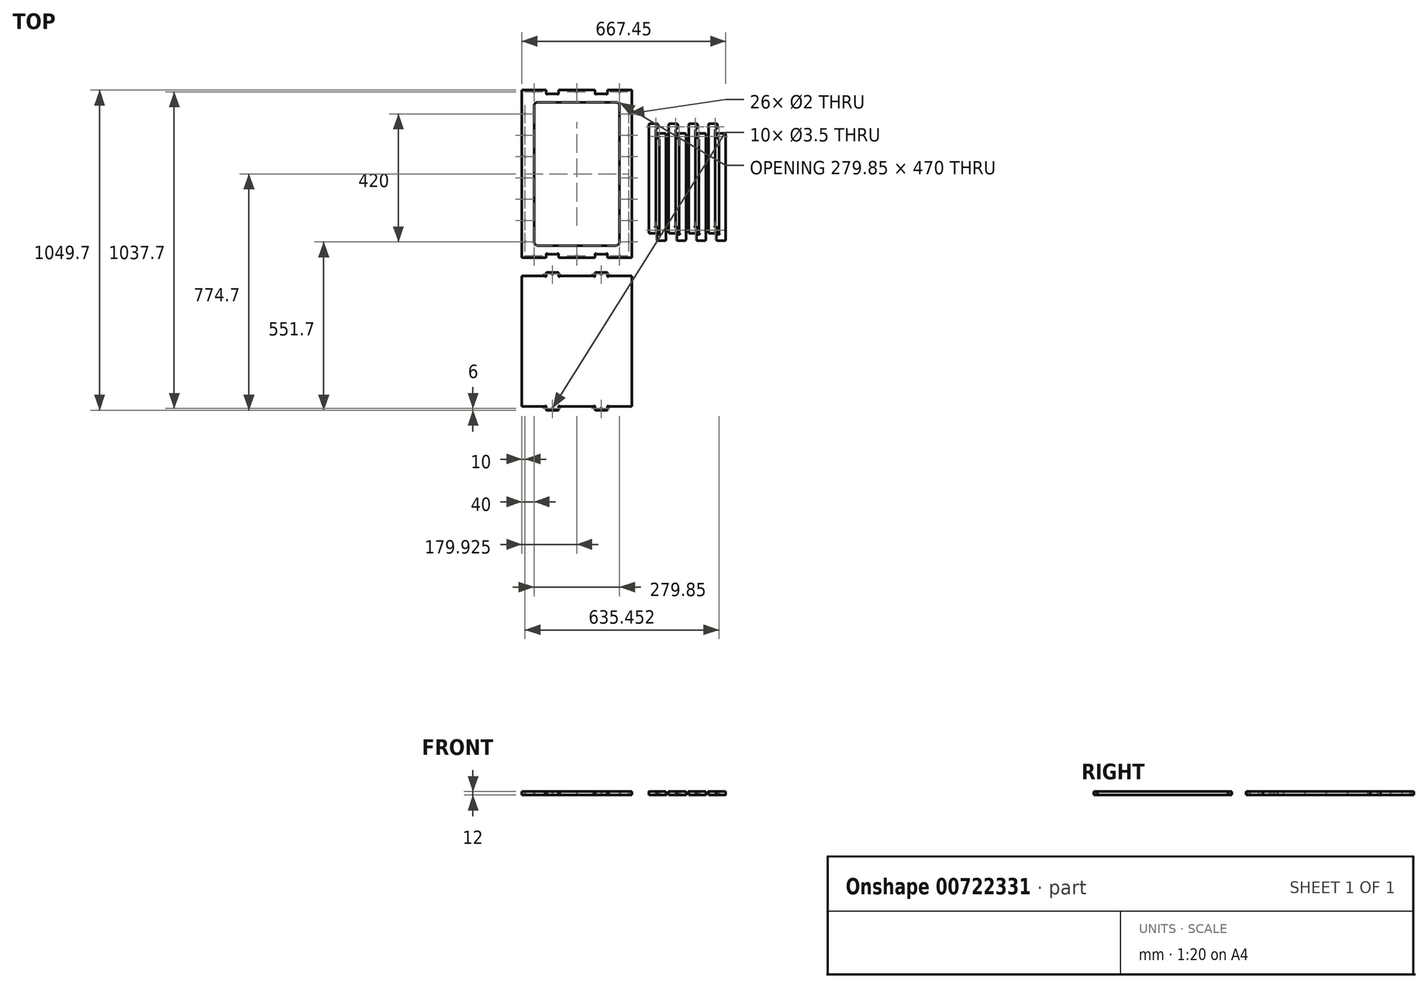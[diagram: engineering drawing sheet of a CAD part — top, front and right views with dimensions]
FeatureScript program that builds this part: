
annotation { "Feature Type Name" : "Feature", "Feature Type Description" : "" }
export const myFeature = defineFeature(function(context is Context, id is Id, definition is map)
    precondition{}
    {
        {
            var Q0;
            Q0=qCreatedBy(makeId("Top.planeOp"),FACE);
            var sketch = newSketch(context, id + "F0", { "sketchPlane" : qUnion([Q0])});
            skLineSegment(sketch, "E0.bottom", {"start": v(0, 0) * mm, "end": v(359.85, 0) * mm});
            skLineSegment(sketch, "E0.top", {"start": v(0, 550) * mm, "end": v(359.85, 550) * mm});
            skLineSegment(sketch, "E0.left", {"start": v(0, 0) * mm, "end": v(0, 550) * mm});
            skLineSegment(sketch, "E0.right", {"start": v(359.85, 0) * mm, "end": v(359.85, 550) * mm});
            skLineSegment(sketch, "E1", {"start": v(40, 550) * mm, "end": v(40, 0) * mm, "construction": true});
            skLineSegment(sketch, "E2", {"start": v(319.85, 0) * mm, "end": v(319.85, 550) * mm, "construction": true});
            skLineSegment(sketch, "E3", {"start": v(359.85, 510) * mm, "end": v(0, 510) * mm, "construction": true});
            skLineSegment(sketch, "E4", {"start": v(0, 40) * mm, "end": v(359.85, 40) * mm, "construction": true});
            skLineSegment(sketch, "E5", {"start": v(52, 510) * mm, "end": v(307.85, 510) * mm});
            skLineSegment(sketch, "E6", {"start": v(319.85, 498) * mm, "end": v(319.85, 425.14) * mm});
            skLineSegment(sketch, "E7", {"start": v(40, 425.14) * mm, "end": v(40, 498) * mm});
            skLineSegment(sketch, "E8", {"start": v(319.85, 381.14) * mm, "end": v(319.85, 52) * mm});
            skLineSegment(sketch, "E9", {"start": v(307.85, 40) * mm, "end": v(52, 40) * mm});
            skLineSegment(sketch, "E10", {"start": v(40, 52) * mm, "end": v(40, 381.14) * mm});
            skPoint(sketch, "E11.visualSharp", {"position": v(40, 510) * mm});
            skArc(sketch, "E11.filletArc", {"start": v(52, 510) * mm, "mid": v(43.51, 506.49) * mm, "end": v(40, 498) * mm});
            skPoint(sketch, "E12.visualSharp", {"position": v(319.85, 510) * mm});
            skArc(sketch, "E12.filletArc", {"start": v(319.85, 498) * mm, "mid": v(316.34, 506.49) * mm, "end": v(307.85, 510) * mm});
            skPoint(sketch, "E13.visualSharp", {"position": v(319.85, 40) * mm});
            skArc(sketch, "E13.filletArc", {"start": v(307.85, 40) * mm, "mid": v(316.34, 43.51) * mm, "end": v(319.85, 52) * mm});
            skPoint(sketch, "E14.visualSharp", {"position": v(40, 40) * mm});
            skArc(sketch, "E14.filletArc", {"start": v(40, 52) * mm, "mid": v(43.51, 43.51) * mm, "end": v(52, 40) * mm});
            skCircle(sketch, "E15", {"center": v(10, 52) * mm, "radius": 1 * mm});
            skLineSegment(sketch, "E16", {"start": v(-24.67, 52) * mm, "end": v(376.85, 52) * mm, "construction": true});
            skCircle(sketch, "E17", {"center": v(349.85, 52) * mm, "radius": 1 * mm});
            skCircle(sketch, "E18.0.1.0", {"center": v(10, 122) * mm, "radius": 1 * mm});
            skCircle(sketch, "E18.0.1.1", {"center": v(349.85, 122) * mm, "radius": 1 * mm});
            skCircle(sketch, "E18.0.2.0", {"center": v(10, 192) * mm, "radius": 1 * mm});
            skCircle(sketch, "E18.0.2.1", {"center": v(349.85, 192) * mm, "radius": 1 * mm});
            skCircle(sketch, "E18.0.3.0", {"center": v(10, 262) * mm, "radius": 1 * mm});
            skCircle(sketch, "E18.0.3.1", {"center": v(349.85, 262) * mm, "radius": 1 * mm});
            skCircle(sketch, "E18.0.4.0", {"center": v(10, 332) * mm, "radius": 1 * mm});
            skCircle(sketch, "E18.0.4.1", {"center": v(349.85, 332) * mm, "radius": 1 * mm});
            skCircle(sketch, "E18.0.5.0", {"center": v(10, 402) * mm, "radius": 1 * mm});
            skCircle(sketch, "E18.0.5.1", {"center": v(349.85, 402) * mm, "radius": 1 * mm});
            skCircle(sketch, "E18.0.6.0", {"center": v(10, 472) * mm, "radius": 1 * mm});
            skCircle(sketch, "E18.0.6.1", {"center": v(349.85, 472) * mm, "radius": 1 * mm});
            skLineSegment(sketch, "E18.direction1", {"start": v(10, 52) * mm, "end": v(35, 52) * mm, "construction": true});
            skLineSegment(sketch, "E18.direction2", {"start": v(10, 52) * mm, "end": v(10, 122) * mm, "construction": true});
            skLineSegment(sketch, "E19", {"start": v(80, 0) * mm, "end": v(80, 12) * mm});
            skLineSegment(sketch, "E20", {"start": v(120, 12) * mm, "end": v(120, 0) * mm});
            skLineSegment(sketch, "E21", {"start": v(239.85, 0) * mm, "end": v(239.85, 12) * mm});
            skLineSegment(sketch, "E22", {"start": v(279.85, 12) * mm, "end": v(279.85, 0) * mm});
            skLineSegment(sketch, "E23", {"start": v(80, 550) * mm, "end": v(80, 538) * mm});
            skLineSegment(sketch, "E24", {"start": v(120, 538) * mm, "end": v(120, 550) * mm});
            skLineSegment(sketch, "E25", {"start": v(239.85, 550) * mm, "end": v(239.85, 538) * mm});
            skLineSegment(sketch, "E26", {"start": v(243.85, 538) * mm, "end": v(275.85, 538) * mm});
            skLineSegment(sketch, "E27", {"start": v(279.85, 538) * mm, "end": v(279.85, 550) * mm});
            skLineSegment(sketch, "E28", {"start": v(0, 6) * mm, "end": v(359.85, 6) * mm, "construction": true});
            skCircle(sketch, "E29", {"center": v(179.93, 6) * mm, "radius": 1.75 * mm});
            skCircle(sketch, "E30", {"center": v(319.85, 6) * mm, "radius": 1.75 * mm});
            skCircle(sketch, "E31", {"center": v(40, 6) * mm, "radius": 1.75 * mm});
            skLineSegment(sketch, "E32", {"start": v(0, 544) * mm, "end": v(359.85, 544) * mm, "construction": true});
            skCircle(sketch, "E33", {"center": v(179.93, 544) * mm, "radius": 1.75 * mm});
            skCircle(sketch, "E34", {"center": v(319.85, 544) * mm, "radius": 1.75 * mm});
            skCircle(sketch, "E35", {"center": v(40, 544) * mm, "radius": 1.75 * mm});
            skArc(sketch, "E36", {"start": v(80, 12) * mm, "mid": v(82, 14) * mm, "end": v(84, 12) * mm});
            skArc(sketch, "E37", {"start": v(120, 12) * mm, "mid": v(118, 14) * mm, "end": v(116, 12) * mm});
            skArc(sketch, "E38", {"start": v(239.85, 12) * mm, "mid": v(241.85, 14) * mm, "end": v(243.85, 12) * mm});
            skArc(sketch, "E39", {"start": v(279.85, 12) * mm, "mid": v(277.85, 14) * mm, "end": v(275.85, 12) * mm});
            skLineSegment(sketch, "E40.trimOffspring", {"start": v(243.85, 12) * mm, "end": v(275.85, 12) * mm});
            skLineSegment(sketch, "E41.trimOffspring", {"start": v(84, 12) * mm, "end": v(116, 12) * mm});
            skArc(sketch, "E42", {"start": v(80, 538) * mm, "mid": v(82, 536) * mm, "end": v(84, 538) * mm});
            skArc(sketch, "E43", {"start": v(120, 538) * mm, "mid": v(118, 536) * mm, "end": v(116, 538) * mm});
            skArc(sketch, "E44", {"start": v(239.85, 538) * mm, "mid": v(241.85, 536) * mm, "end": v(243.85, 538) * mm});
            skArc(sketch, "E45", {"start": v(279.85, 538) * mm, "mid": v(277.85, 536) * mm, "end": v(275.85, 538) * mm});
            skLineSegment(sketch, "E46.trimOffspring", {"start": v(84, 538) * mm, "end": v(116, 538) * mm});
            skLineSegment(sketch, "E47", {"start": v(40, 425.14) * mm, "end": v(40, 381.14) * mm});
            skLineSegment(sketch, "E48", {"start": v(319.85, 425.14) * mm, "end": v(319.85, 381.14) * mm});
            skLineSegment(sketch, "E49", {"start": v(416.45, 83.42) * mm, "end": v(416.45, 436.47) * mm});
            skLineSegment(sketch, "E50", {"start": v(419.85, 439.87) * mm, "end": v(441.45, 439.87) * mm});
            skLineSegment(sketch, "E51", {"start": v(446.45, 434.87) * mm, "end": v(446.45, 429.28) * mm});
            skLineSegment(sketch, "E52", {"start": v(445.46, 426.87) * mm, "end": v(439.45, 420.86) * mm});
            skLineSegment(sketch, "E53", {"start": v(438.45, 418.46) * mm, "end": v(438.45, 100.02) * mm});
            skLineSegment(sketch, "E54", {"start": v(438.45, 100.02) * mm, "end": v(443.05, 100.02) * mm});
            skLineSegment(sketch, "E55", {"start": v(446.45, 96.62) * mm, "end": v(446.45, 83.42) * mm});
            skLineSegment(sketch, "E56", {"start": v(443.05, 80.02) * mm, "end": v(419.85, 80.02) * mm});
            skArc(sketch, "E57", {"start": v(438.45, 104.02) * mm, "mid": v(436.45, 102.02) * mm, "end": v(438.45, 100.02) * mm});
            skPoint(sketch, "E58.visualSharp", {"position": v(446.45, 100.02) * mm});
            skArc(sketch, "E58.filletArc", {"start": v(446.45, 96.62) * mm, "mid": v(445.46, 99.02) * mm, "end": v(443.05, 100.02) * mm});
            skPoint(sketch, "E59.visualSharp", {"position": v(446.45, 80.02) * mm});
            skArc(sketch, "E59.filletArc", {"start": v(443.05, 80.02) * mm, "mid": v(445.46, 81.01) * mm, "end": v(446.45, 83.42) * mm});
            skPoint(sketch, "E60.visualSharp", {"position": v(416.45, 80.02) * mm});
            skArc(sketch, "E60.filletArc", {"start": v(416.45, 83.42) * mm, "mid": v(417.45, 81.01) * mm, "end": v(419.85, 80.02) * mm});
            skPoint(sketch, "E61.visualSharp", {"position": v(416.45, 439.87) * mm});
            skArc(sketch, "E61.filletArc", {"start": v(419.85, 439.87) * mm, "mid": v(417.45, 438.87) * mm, "end": v(416.45, 436.47) * mm});
            skPoint(sketch, "E62.visualSharp", {"position": v(446.45, 427.87) * mm});
            skArc(sketch, "E62.filletArc", {"start": v(445.46, 426.87) * mm, "mid": v(446.2, 427.97) * mm, "end": v(446.45, 429.28) * mm});
            skPoint(sketch, "E63.visualSharp", {"position": v(438.45, 419.87) * mm});
            skArc(sketch, "E63.filletArc", {"start": v(439.45, 420.86) * mm, "mid": v(438.71, 419.76) * mm, "end": v(438.45, 418.46) * mm});
            skCircle(sketch, "E64", {"center": v(438.45, 90.02) * mm, "radius": 1 * mm});
            skPoint(sketch, "E65.visualSharp", {"position": v(446.45, 439.87) * mm});
            skArc(sketch, "E65.filletArc", {"start": v(446.45, 434.87) * mm, "mid": v(444.99, 438.4) * mm, "end": v(441.45, 439.87) * mm});
            skCircle(sketch, "E66", {"center": v(438.45, 429.87) * mm, "radius": 1 * mm});
            skLineSegment(sketch, "E67", {"start": v(445.85, 407.87) * mm, "end": v(469.05, 407.87) * mm});
            skLineSegment(sketch, "E68", {"start": v(472.45, 404.47) * mm, "end": v(472.45, 59.42) * mm});
            skLineSegment(sketch, "E69", {"start": v(469.05, 56.02) * mm, "end": v(445.85, 56.02) * mm});
            skLineSegment(sketch, "E70", {"start": v(442.45, 59.42) * mm, "end": v(442.45, 72.62) * mm});
            skLineSegment(sketch, "E71", {"start": v(445.85, 76.02) * mm, "end": v(450.45, 76.02) * mm});
            skLineSegment(sketch, "E72", {"start": v(450.45, 76.02) * mm, "end": v(450.45, 386.46) * mm});
            skLineSegment(sketch, "E73", {"start": v(449.46, 388.86) * mm, "end": v(443.45, 394.87) * mm});
            skLineSegment(sketch, "E74", {"start": v(442.45, 397.28) * mm, "end": v(442.45, 404.47) * mm});
            skPoint(sketch, "E75.visualSharp", {"position": v(442.45, 395.87) * mm});
            skArc(sketch, "E75.filletArc", {"start": v(442.45, 397.28) * mm, "mid": v(442.71, 395.97) * mm, "end": v(443.45, 394.87) * mm});
            skPoint(sketch, "E76.visualSharp", {"position": v(450.45, 387.87) * mm});
            skArc(sketch, "E76.filletArc", {"start": v(450.45, 386.46) * mm, "mid": v(450.2, 387.76) * mm, "end": v(449.46, 388.86) * mm});
            skPoint(sketch, "E77.visualSharp", {"position": v(442.45, 407.87) * mm});
            skArc(sketch, "E77.filletArc", {"start": v(445.85, 407.87) * mm, "mid": v(443.45, 406.87) * mm, "end": v(442.45, 404.47) * mm});
            skPoint(sketch, "E78.visualSharp", {"position": v(472.45, 407.87) * mm});
            skArc(sketch, "E78.filletArc", {"start": v(472.45, 404.47) * mm, "mid": v(471.46, 406.87) * mm, "end": v(469.05, 407.87) * mm});
            skPoint(sketch, "E79.visualSharp", {"position": v(472.45, 56.02) * mm});
            skArc(sketch, "E79.filletArc", {"start": v(469.05, 56.02) * mm, "mid": v(471.46, 57.01) * mm, "end": v(472.45, 59.42) * mm});
            skPoint(sketch, "E80.visualSharp", {"position": v(442.45, 56.02) * mm});
            skArc(sketch, "E80.filletArc", {"start": v(442.45, 59.42) * mm, "mid": v(443.45, 57.01) * mm, "end": v(445.85, 56.02) * mm});
            skPoint(sketch, "E81.visualSharp", {"position": v(442.45, 76.02) * mm});
            skArc(sketch, "E81.filletArc", {"start": v(445.85, 76.02) * mm, "mid": v(443.45, 75.02) * mm, "end": v(442.45, 72.62) * mm});
            skArc(sketch, "E82", {"start": v(450.45, 76.02) * mm, "mid": v(452.45, 78.02) * mm, "end": v(450.45, 80.02) * mm});
            skLineSegment(sketch, "E83.1.0.0", {"start": v(515.45, 76.02) * mm, "end": v(515.45, 386.46) * mm});
            skPoint(sketch, "E83.1.0.1", {"position": v(507.45, 56.02) * mm});
            skPoint(sketch, "E83.1.0.2", {"position": v(503.45, 419.87) * mm});
            skPoint(sketch, "E83.1.0.3", {"position": v(515.45, 387.87) * mm});
            skPoint(sketch, "E83.1.0.4", {"position": v(511.45, 80.02) * mm});
            skLineSegment(sketch, "E83.1.0.5", {"start": v(511.45, 96.62) * mm, "end": v(511.45, 83.42) * mm});
            skLineSegment(sketch, "E83.1.0.6", {"start": v(534.05, 56.02) * mm, "end": v(510.85, 56.02) * mm});
            skPoint(sketch, "E83.1.0.7", {"position": v(537.45, 56.02) * mm});
            skPoint(sketch, "E83.1.0.8", {"position": v(511.45, 427.87) * mm});
            skLineSegment(sketch, "E83.1.0.9", {"start": v(508.05, 80.02) * mm, "end": v(484.85, 80.02) * mm});
            skLineSegment(sketch, "E83.1.0.10", {"start": v(481.45, 83.42) * mm, "end": v(481.45, 436.47) * mm});
            skLineSegment(sketch, "E83.1.0.11", {"start": v(510.85, 407.87) * mm, "end": v(534.05, 407.87) * mm});
            skPoint(sketch, "E83.1.0.12", {"position": v(507.45, 76.02) * mm});
            skLineSegment(sketch, "E83.1.0.13", {"start": v(507.45, 59.42) * mm, "end": v(507.45, 72.62) * mm});
            skPoint(sketch, "E83.1.0.14", {"position": v(507.45, 407.87) * mm});
            skPoint(sketch, "E83.1.0.15", {"position": v(481.45, 80.02) * mm});
            skPoint(sketch, "E83.1.0.16", {"position": v(507.45, 395.87) * mm});
            skPoint(sketch, "E83.1.0.17", {"position": v(511.45, 100.02) * mm});
            skLineSegment(sketch, "E83.1.0.18", {"start": v(484.85, 439.87) * mm, "end": v(506.45, 439.87) * mm});
            skLineSegment(sketch, "E83.1.0.19", {"start": v(537.45, 404.47) * mm, "end": v(537.45, 59.42) * mm});
            skPoint(sketch, "E83.1.0.20", {"position": v(537.45, 407.87) * mm});
            skPoint(sketch, "E83.1.0.21", {"position": v(481.45, 439.87) * mm});
            skPoint(sketch, "E83.1.0.22", {"position": v(511.45, 439.87) * mm});
            skLineSegment(sketch, "E83.1.0.23", {"start": v(503.45, 418.46) * mm, "end": v(503.45, 100.02) * mm});
            skCircle(sketch, "E83.1.0.24", {"center": v(503.45, 429.87) * mm, "radius": 1 * mm});
            skCircle(sketch, "E83.1.0.25", {"center": v(503.45, 90.02) * mm, "radius": 1 * mm});
            skArc(sketch, "E83.1.0.26", {"start": v(534.05, 56.02) * mm, "mid": v(536.46, 57.01) * mm, "end": v(537.45, 59.42) * mm});
            skArc(sketch, "E83.1.0.27", {"start": v(507.45, 59.42) * mm, "mid": v(508.45, 57.01) * mm, "end": v(510.85, 56.02) * mm});
            skLineSegment(sketch, "E83.1.0.28", {"start": v(511.45, 434.87) * mm, "end": v(511.45, 429.28) * mm});
            skArc(sketch, "E83.1.0.29", {"start": v(508.05, 80.02) * mm, "mid": v(510.46, 81.01) * mm, "end": v(511.45, 83.42) * mm});
            skArc(sketch, "E83.1.0.30", {"start": v(515.45, 76.02) * mm, "mid": v(517.45, 78.02) * mm, "end": v(515.45, 80.02) * mm});
            skArc(sketch, "E83.1.0.31", {"start": v(511.45, 434.87) * mm, "mid": v(509.99, 438.4) * mm, "end": v(506.45, 439.87) * mm});
            skArc(sketch, "E83.1.0.32", {"start": v(537.45, 404.47) * mm, "mid": v(536.46, 406.87) * mm, "end": v(534.05, 407.87) * mm});
            skArc(sketch, "E83.1.0.33", {"start": v(481.45, 83.42) * mm, "mid": v(482.45, 81.01) * mm, "end": v(484.85, 80.02) * mm});
            skArc(sketch, "E83.1.0.34", {"start": v(503.45, 104.02) * mm, "mid": v(501.45, 102.02) * mm, "end": v(503.45, 100.02) * mm});
            skArc(sketch, "E83.1.0.35", {"start": v(484.85, 439.87) * mm, "mid": v(482.45, 438.87) * mm, "end": v(481.45, 436.47) * mm});
            skLineSegment(sketch, "E83.1.0.36", {"start": v(503.45, 100.02) * mm, "end": v(508.05, 100.02) * mm});
            skArc(sketch, "E83.1.0.37", {"start": v(510.46, 426.87) * mm, "mid": v(511.2, 427.97) * mm, "end": v(511.45, 429.28) * mm});
            skArc(sketch, "E83.1.0.38", {"start": v(515.45, 386.46) * mm, "mid": v(515.2, 387.76) * mm, "end": v(514.46, 388.86) * mm});
            skArc(sketch, "E83.1.0.39", {"start": v(511.45, 96.62) * mm, "mid": v(510.46, 99.02) * mm, "end": v(508.05, 100.02) * mm});
            skLineSegment(sketch, "E83.1.0.40", {"start": v(514.46, 388.86) * mm, "end": v(508.45, 394.87) * mm});
            skArc(sketch, "E83.1.0.41", {"start": v(510.85, 76.02) * mm, "mid": v(508.45, 75.02) * mm, "end": v(507.45, 72.62) * mm});
            skArc(sketch, "E83.1.0.42", {"start": v(504.45, 420.86) * mm, "mid": v(503.71, 419.76) * mm, "end": v(503.45, 418.46) * mm});
            skArc(sketch, "E83.1.0.43", {"start": v(510.85, 407.87) * mm, "mid": v(508.45, 406.87) * mm, "end": v(507.45, 404.47) * mm});
            skLineSegment(sketch, "E83.1.0.44", {"start": v(507.45, 397.28) * mm, "end": v(507.45, 404.47) * mm});
            skLineSegment(sketch, "E83.1.0.45", {"start": v(510.46, 426.87) * mm, "end": v(504.45, 420.86) * mm});
            skArc(sketch, "E83.1.0.46", {"start": v(507.45, 397.28) * mm, "mid": v(507.71, 395.97) * mm, "end": v(508.45, 394.87) * mm});
            skLineSegment(sketch, "E83.1.0.47", {"start": v(510.85, 76.02) * mm, "end": v(515.45, 76.02) * mm});
            skLineSegment(sketch, "E83.2.0.0", {"start": v(580.45, 76.02) * mm, "end": v(580.45, 386.46) * mm});
            skPoint(sketch, "E83.2.0.1", {"position": v(572.45, 56.02) * mm});
            skPoint(sketch, "E83.2.0.2", {"position": v(568.45, 419.87) * mm});
            skPoint(sketch, "E83.2.0.3", {"position": v(580.45, 387.87) * mm});
            skPoint(sketch, "E83.2.0.4", {"position": v(576.45, 80.02) * mm});
            skLineSegment(sketch, "E83.2.0.5", {"start": v(576.45, 96.62) * mm, "end": v(576.45, 83.42) * mm});
            skLineSegment(sketch, "E83.2.0.6", {"start": v(599.05, 56.02) * mm, "end": v(575.85, 56.02) * mm});
            skPoint(sketch, "E83.2.0.7", {"position": v(602.45, 56.02) * mm});
            skPoint(sketch, "E83.2.0.8", {"position": v(576.45, 427.87) * mm});
            skLineSegment(sketch, "E83.2.0.9", {"start": v(573.05, 80.02) * mm, "end": v(549.85, 80.02) * mm});
            skLineSegment(sketch, "E83.2.0.10", {"start": v(546.45, 83.42) * mm, "end": v(546.45, 436.47) * mm});
            skLineSegment(sketch, "E83.2.0.11", {"start": v(575.85, 407.87) * mm, "end": v(599.05, 407.87) * mm});
            skPoint(sketch, "E83.2.0.12", {"position": v(572.45, 76.02) * mm});
            skLineSegment(sketch, "E83.2.0.13", {"start": v(572.45, 59.42) * mm, "end": v(572.45, 72.62) * mm});
            skPoint(sketch, "E83.2.0.14", {"position": v(572.45, 407.87) * mm});
            skPoint(sketch, "E83.2.0.15", {"position": v(546.45, 80.02) * mm});
            skPoint(sketch, "E83.2.0.16", {"position": v(572.45, 395.87) * mm});
            skPoint(sketch, "E83.2.0.17", {"position": v(576.45, 100.02) * mm});
            skLineSegment(sketch, "E83.2.0.18", {"start": v(549.85, 439.87) * mm, "end": v(571.45, 439.87) * mm});
            skLineSegment(sketch, "E83.2.0.19", {"start": v(602.45, 404.47) * mm, "end": v(602.45, 59.42) * mm});
            skPoint(sketch, "E83.2.0.20", {"position": v(602.45, 407.87) * mm});
            skPoint(sketch, "E83.2.0.21", {"position": v(546.45, 439.87) * mm});
            skPoint(sketch, "E83.2.0.22", {"position": v(576.45, 439.87) * mm});
            skLineSegment(sketch, "E83.2.0.23", {"start": v(568.45, 418.46) * mm, "end": v(568.45, 100.02) * mm});
            skCircle(sketch, "E83.2.0.24", {"center": v(568.45, 429.87) * mm, "radius": 1 * mm});
            skCircle(sketch, "E83.2.0.25", {"center": v(568.45, 90.02) * mm, "radius": 1 * mm});
            skArc(sketch, "E83.2.0.26", {"start": v(599.05, 56.02) * mm, "mid": v(601.46, 57.01) * mm, "end": v(602.45, 59.42) * mm});
            skArc(sketch, "E83.2.0.27", {"start": v(572.45, 59.42) * mm, "mid": v(573.45, 57.01) * mm, "end": v(575.85, 56.02) * mm});
            skLineSegment(sketch, "E83.2.0.28", {"start": v(576.45, 434.87) * mm, "end": v(576.45, 429.28) * mm});
            skArc(sketch, "E83.2.0.29", {"start": v(573.05, 80.02) * mm, "mid": v(575.46, 81.01) * mm, "end": v(576.45, 83.42) * mm});
            skArc(sketch, "E83.2.0.30", {"start": v(580.45, 76.02) * mm, "mid": v(582.45, 78.02) * mm, "end": v(580.45, 80.02) * mm});
            skArc(sketch, "E83.2.0.31", {"start": v(576.45, 434.87) * mm, "mid": v(574.99, 438.4) * mm, "end": v(571.45, 439.87) * mm});
            skArc(sketch, "E83.2.0.32", {"start": v(602.45, 404.47) * mm, "mid": v(601.46, 406.87) * mm, "end": v(599.05, 407.87) * mm});
            skArc(sketch, "E83.2.0.33", {"start": v(546.45, 83.42) * mm, "mid": v(547.45, 81.01) * mm, "end": v(549.85, 80.02) * mm});
            skArc(sketch, "E83.2.0.34", {"start": v(568.45, 104.02) * mm, "mid": v(566.45, 102.02) * mm, "end": v(568.45, 100.02) * mm});
            skArc(sketch, "E83.2.0.35", {"start": v(549.85, 439.87) * mm, "mid": v(547.45, 438.87) * mm, "end": v(546.45, 436.47) * mm});
            skLineSegment(sketch, "E83.2.0.36", {"start": v(568.45, 100.02) * mm, "end": v(573.05, 100.02) * mm});
            skArc(sketch, "E83.2.0.37", {"start": v(575.46, 426.87) * mm, "mid": v(576.2, 427.97) * mm, "end": v(576.45, 429.28) * mm});
            skArc(sketch, "E83.2.0.38", {"start": v(580.45, 386.46) * mm, "mid": v(580.2, 387.76) * mm, "end": v(579.46, 388.86) * mm});
            skArc(sketch, "E83.2.0.39", {"start": v(576.45, 96.62) * mm, "mid": v(575.46, 99.02) * mm, "end": v(573.05, 100.02) * mm});
            skLineSegment(sketch, "E83.2.0.40", {"start": v(579.46, 388.86) * mm, "end": v(573.45, 394.87) * mm});
            skArc(sketch, "E83.2.0.41", {"start": v(575.85, 76.02) * mm, "mid": v(573.45, 75.02) * mm, "end": v(572.45, 72.62) * mm});
            skArc(sketch, "E83.2.0.42", {"start": v(569.45, 420.86) * mm, "mid": v(568.71, 419.76) * mm, "end": v(568.45, 418.46) * mm});
            skArc(sketch, "E83.2.0.43", {"start": v(575.85, 407.87) * mm, "mid": v(573.45, 406.87) * mm, "end": v(572.45, 404.47) * mm});
            skLineSegment(sketch, "E83.2.0.44", {"start": v(572.45, 397.28) * mm, "end": v(572.45, 404.47) * mm});
            skLineSegment(sketch, "E83.2.0.45", {"start": v(575.46, 426.87) * mm, "end": v(569.45, 420.86) * mm});
            skArc(sketch, "E83.2.0.46", {"start": v(572.45, 397.28) * mm, "mid": v(572.71, 395.97) * mm, "end": v(573.45, 394.87) * mm});
            skLineSegment(sketch, "E83.2.0.47", {"start": v(575.85, 76.02) * mm, "end": v(580.45, 76.02) * mm});
            skLineSegment(sketch, "E83.3.0.0", {"start": v(645.45, 76.02) * mm, "end": v(645.45, 386.46) * mm});
            skPoint(sketch, "E83.3.0.1", {"position": v(637.45, 56.02) * mm});
            skPoint(sketch, "E83.3.0.2", {"position": v(633.45, 419.87) * mm});
            skPoint(sketch, "E83.3.0.3", {"position": v(645.45, 387.87) * mm});
            skPoint(sketch, "E83.3.0.4", {"position": v(641.45, 80.02) * mm});
            skLineSegment(sketch, "E83.3.0.5", {"start": v(641.45, 96.62) * mm, "end": v(641.45, 83.42) * mm});
            skLineSegment(sketch, "E83.3.0.6", {"start": v(664.05, 56.02) * mm, "end": v(640.85, 56.02) * mm});
            skPoint(sketch, "E83.3.0.7", {"position": v(667.45, 56.02) * mm});
            skPoint(sketch, "E83.3.0.8", {"position": v(641.45, 427.87) * mm});
            skLineSegment(sketch, "E83.3.0.9", {"start": v(638.05, 80.02) * mm, "end": v(614.85, 80.02) * mm});
            skLineSegment(sketch, "E83.3.0.10", {"start": v(611.45, 83.42) * mm, "end": v(611.45, 436.47) * mm});
            skLineSegment(sketch, "E83.3.0.11", {"start": v(640.85, 407.87) * mm, "end": v(664.05, 407.87) * mm});
            skPoint(sketch, "E83.3.0.12", {"position": v(637.45, 76.02) * mm});
            skLineSegment(sketch, "E83.3.0.13", {"start": v(637.45, 59.42) * mm, "end": v(637.45, 72.62) * mm});
            skPoint(sketch, "E83.3.0.14", {"position": v(637.45, 407.87) * mm});
            skPoint(sketch, "E83.3.0.15", {"position": v(611.45, 80.02) * mm});
            skPoint(sketch, "E83.3.0.16", {"position": v(637.45, 395.87) * mm});
            skPoint(sketch, "E83.3.0.17", {"position": v(641.45, 100.02) * mm});
            skLineSegment(sketch, "E83.3.0.18", {"start": v(614.85, 439.87) * mm, "end": v(636.45, 439.87) * mm});
            skLineSegment(sketch, "E83.3.0.19", {"start": v(667.45, 404.47) * mm, "end": v(667.45, 59.42) * mm});
            skPoint(sketch, "E83.3.0.20", {"position": v(667.45, 407.87) * mm});
            skPoint(sketch, "E83.3.0.21", {"position": v(611.45, 439.87) * mm});
            skPoint(sketch, "E83.3.0.22", {"position": v(641.45, 439.87) * mm});
            skLineSegment(sketch, "E83.3.0.23", {"start": v(633.45, 418.46) * mm, "end": v(633.45, 100.02) * mm});
            skCircle(sketch, "E83.3.0.24", {"center": v(633.45, 429.87) * mm, "radius": 1 * mm});
            skCircle(sketch, "E83.3.0.25", {"center": v(633.45, 90.02) * mm, "radius": 1 * mm});
            skArc(sketch, "E83.3.0.26", {"start": v(664.05, 56.02) * mm, "mid": v(666.46, 57.01) * mm, "end": v(667.45, 59.42) * mm});
            skArc(sketch, "E83.3.0.27", {"start": v(637.45, 59.42) * mm, "mid": v(638.45, 57.01) * mm, "end": v(640.85, 56.02) * mm});
            skLineSegment(sketch, "E83.3.0.28", {"start": v(641.45, 434.87) * mm, "end": v(641.45, 429.28) * mm});
            skArc(sketch, "E83.3.0.29", {"start": v(638.05, 80.02) * mm, "mid": v(640.46, 81.01) * mm, "end": v(641.45, 83.42) * mm});
            skArc(sketch, "E83.3.0.30", {"start": v(645.45, 76.02) * mm, "mid": v(647.45, 78.02) * mm, "end": v(645.45, 80.02) * mm});
            skArc(sketch, "E83.3.0.31", {"start": v(641.45, 434.87) * mm, "mid": v(639.99, 438.4) * mm, "end": v(636.45, 439.87) * mm});
            skArc(sketch, "E83.3.0.32", {"start": v(667.45, 404.47) * mm, "mid": v(666.46, 406.87) * mm, "end": v(664.05, 407.87) * mm});
            skArc(sketch, "E83.3.0.33", {"start": v(611.45, 83.42) * mm, "mid": v(612.45, 81.01) * mm, "end": v(614.85, 80.02) * mm});
            skArc(sketch, "E83.3.0.34", {"start": v(633.45, 104.02) * mm, "mid": v(631.45, 102.02) * mm, "end": v(633.45, 100.02) * mm});
            skArc(sketch, "E83.3.0.35", {"start": v(614.85, 439.87) * mm, "mid": v(612.45, 438.87) * mm, "end": v(611.45, 436.47) * mm});
            skLineSegment(sketch, "E83.3.0.36", {"start": v(633.45, 100.02) * mm, "end": v(638.05, 100.02) * mm});
            skArc(sketch, "E83.3.0.37", {"start": v(640.46, 426.87) * mm, "mid": v(641.2, 427.97) * mm, "end": v(641.45, 429.28) * mm});
            skArc(sketch, "E83.3.0.38", {"start": v(645.45, 386.46) * mm, "mid": v(645.2, 387.76) * mm, "end": v(644.46, 388.86) * mm});
            skArc(sketch, "E83.3.0.39", {"start": v(641.45, 96.62) * mm, "mid": v(640.46, 99.02) * mm, "end": v(638.05, 100.02) * mm});
            skLineSegment(sketch, "E83.3.0.40", {"start": v(644.46, 388.86) * mm, "end": v(638.45, 394.87) * mm});
            skArc(sketch, "E83.3.0.41", {"start": v(640.85, 76.02) * mm, "mid": v(638.45, 75.02) * mm, "end": v(637.45, 72.62) * mm});
            skArc(sketch, "E83.3.0.42", {"start": v(634.45, 420.86) * mm, "mid": v(633.71, 419.76) * mm, "end": v(633.45, 418.46) * mm});
            skArc(sketch, "E83.3.0.43", {"start": v(640.85, 407.87) * mm, "mid": v(638.45, 406.87) * mm, "end": v(637.45, 404.47) * mm});
            skLineSegment(sketch, "E83.3.0.44", {"start": v(637.45, 397.28) * mm, "end": v(637.45, 404.47) * mm});
            skLineSegment(sketch, "E83.3.0.45", {"start": v(640.46, 426.87) * mm, "end": v(634.45, 420.86) * mm});
            skArc(sketch, "E83.3.0.46", {"start": v(637.45, 397.28) * mm, "mid": v(637.71, 395.97) * mm, "end": v(638.45, 394.87) * mm});
            skLineSegment(sketch, "E83.3.0.47", {"start": v(640.85, 76.02) * mm, "end": v(645.45, 76.02) * mm});
            skLineSegment(sketch, "E83.direction1", {"start": v(416.45, 80.02) * mm, "end": v(481.45, 80.02) * mm, "construction": true});
            skCircle(sketch, "E84", {"center": v(450.45, 397.87) * mm, "radius": 1 * mm});
            skCircle(sketch, "E85.1.0.0", {"center": v(515.45, 397.87) * mm, "radius": 1 * mm});
            skCircle(sketch, "E85.2.0.0", {"center": v(580.45, 397.87) * mm, "radius": 1 * mm});
            skCircle(sketch, "E85.3.0.0", {"center": v(645.45, 397.87) * mm, "radius": 1 * mm});
            skLineSegment(sketch, "E85.direction1", {"start": v(450.45, 397.87) * mm, "end": v(515.45, 397.87) * mm, "construction": true});
            skLineSegment(sketch, "E86", {"start": v(50, 500) * mm, "end": v(138, 500) * mm});
            skLineSegment(sketch, "E87", {"start": v(138, 500) * mm, "end": v(138, 488) * mm});
            skLineSegment(sketch, "E88", {"start": v(100, 320) * mm, "end": v(50, 320) * mm});
            skLineSegment(sketch, "E89", {"start": v(50, 320) * mm, "end": v(50, 500) * mm});
            skLineSegment(sketch, "E90.MirrorCS", {"start": v(50, 320) * mm, "end": v(50, 140) * mm});
            skLineSegment(sketch, "E91.MirrorCS", {"start": v(138, 140) * mm, "end": v(138, 152) * mm});
            skLineSegment(sketch, "E92.MirrorCS", {"start": v(50, 140) * mm, "end": v(138, 140) * mm});
            skLineSegment(sketch, "E93", {"start": v(138, 494) * mm, "end": v(50, 494) * mm, "construction": true});
            skCircle(sketch, "E94", {"center": v(62, 494) * mm, "radius": 2.5 * mm});
            skCircle(sketch, "E95", {"center": v(126, 494) * mm, "radius": 2.5 * mm});
            skLineSegment(sketch, "E96", {"start": v(100, 320) * mm, "end": v(100, 212.11) * mm, "construction": true});
            skArc(sketch, "E97", {"start": v(100, 320) * mm, "mid": v(109.62, 406.12) * mm, "end": v(138, 488) * mm});
            skArc(sketch, "E98.MirrorCS", {"start": v(100, 320) * mm, "mid": v(109.62, 233.88) * mm, "end": v(138, 152) * mm});
            skLineSegment(sketch, "E99", {"start": v(144.55, 471.33) * mm, "end": v(144.55, 351.18) * mm});
            skArc(sketch, "E100.MirrorCS", {"start": v(160.1, 231) * mm, "mid": v(150.49, 317.12) * mm, "end": v(122.1, 399) * mm});
            skLineSegment(sketch, "E101.MirrorCS", {"start": v(122.1, 411) * mm, "end": v(122.1, 399) * mm});
            skLineSegment(sketch, "E102.MirrorCS", {"start": v(210.1, 411) * mm, "end": v(122.1, 411) * mm});
            skCircle(sketch, "E103.MirrorC", {"center": v(134.1, 405) * mm, "radius": 1.75 * mm});
            skCircle(sketch, "E104.MirrorC", {"center": v(198.1, 405) * mm, "radius": 1.75 * mm});
            skLineSegment(sketch, "E105.MirrorCS", {"start": v(210.1, 231) * mm, "end": v(210.1, 411) * mm});
            skLineSegment(sketch, "E106.MirrorCS", {"start": v(210.1, 231) * mm, "end": v(210.1, 51) * mm});
            skLineSegment(sketch, "E107.MirrorCS", {"start": v(210.1, 51) * mm, "end": v(122.1, 51) * mm});
            skArc(sketch, "E108.MirrorCS", {"start": v(160.1, 231) * mm, "mid": v(150.49, 144.88) * mm, "end": v(122.1, 63) * mm});
            skLineSegment(sketch, "E109.MirrorCS", {"start": v(122.1, 51) * mm, "end": v(122.1, 63) * mm});
            skSolve(sketch);
        }
        {
            var Q0;
            Q0=makeQuery(id+"F0.imprint","IMPRINT",FACE,{"disambiguationData":[TD([[makeQuery(id+"F0.imprint","IMPRINT",EDGE,{"derivedFrom":sQuery(id+"F0.wireOp",EDGE,"E0.bottom")}),1.0]])]});
            var Q1;
            Q1=makeQuery(id+"F0.imprint","IMPRINT",FACE,{"disambiguationData":[TD([[makeQuery(id+"F0.imprint","IMPRINT",EDGE,{"derivedFrom":sQuery(id+"F0.wireOp",EDGE,"E49")}),-1.0]])]});
            var Q2;
            Q2=makeQuery(id+"F0.imprint","IMPRINT",FACE,{"disambiguationData":[TD([[makeQuery(id+"F0.imprint","IMPRINT",EDGE,{"derivedFrom":sQuery(id+"F0.wireOp",EDGE,"E67")}),-1.0]])]});
            var Q3;
            Q3=makeQuery(id+"F0.imprint","IMPRINT",FACE,{"disambiguationData":[TD([[makeQuery(id+"F0.imprint","IMPRINT",EDGE,{"derivedFrom":sQuery(id+"F0.wireOp",EDGE,"E83.1.0.5")}),-1.0]])]});
            var Q4;
            Q4=makeQuery(id+"F0.imprint","IMPRINT",FACE,{"disambiguationData":[TD([[makeQuery(id+"F0.imprint","IMPRINT",EDGE,{"derivedFrom":sQuery(id+"F0.wireOp",EDGE,"E83.1.0.6")}),-1.0]])]});
            var Q5;
            Q5=makeQuery(id+"F0.imprint","IMPRINT",FACE,{"disambiguationData":[TD([[makeQuery(id+"F0.imprint","IMPRINT",EDGE,{"derivedFrom":sQuery(id+"F0.wireOp",EDGE,"E83.2.0.5")}),-1.0]])]});
            var Q6;
            Q6=makeQuery(id+"F0.imprint","IMPRINT",FACE,{"disambiguationData":[TD([[makeQuery(id+"F0.imprint","IMPRINT",EDGE,{"derivedFrom":sQuery(id+"F0.wireOp",EDGE,"E83.2.0.6")}),-1.0]])]});
            var Q7;
            Q7=makeQuery(id+"F0.imprint","IMPRINT",FACE,{"disambiguationData":[TD([[makeQuery(id+"F0.imprint","IMPRINT",EDGE,{"derivedFrom":sQuery(id+"F0.wireOp",EDGE,"E83.3.0.5")}),-1.0]])]});
            var Q8;
            Q8=makeQuery(id+"F0.imprint","IMPRINT",FACE,{"disambiguationData":[TD([[makeQuery(id+"F0.imprint","IMPRINT",EDGE,{"derivedFrom":sQuery(id+"F0.wireOp",EDGE,"E83.3.0.6")}),-1.0]])]});
            extrude(context, id + "F1", {"entities" : qUnion([Q0, Q1, Q2, Q3, Q4, Q5, Q6, Q7, Q8]), "depth" : 12 * mm, "offsetDistance" : 25 * mm});
        }
        {
            var Q0;
            Q0=qCreatedBy(makeId("Top.planeOp"),FACE);
            var sketch = newSketch(context, id + "F2", { "sketchPlane" : qUnion([Q0])});
            skLineSegment(sketch, "E110", {"start": v(0, -273.7) * mm, "end": v(0, -59.7) * mm});
            skLineSegment(sketch, "E111", {"start": v(0, -59.7) * mm, "end": v(76, -59.7) * mm});
            skLineSegment(sketch, "E112", {"start": v(179.93, -59.7) * mm, "end": v(179.93, -273.7) * mm, "construction": true});
            skLineSegment(sketch, "E113", {"start": v(179.93, -273.7) * mm, "end": v(0, -273.7) * mm, "construction": true});
            skLineSegment(sketch, "E114.top", {"start": v(80, -47.7) * mm, "end": v(120, -47.7) * mm});
            skLineSegment(sketch, "E114.left", {"start": v(80, -59.7) * mm, "end": v(80, -47.7) * mm});
            skLineSegment(sketch, "E114.right", {"start": v(120, -59.7) * mm, "end": v(120, -47.7) * mm});
            skLineSegment(sketch, "E115.trimOffspring", {"start": v(124, -59.7) * mm, "end": v(179.93, -59.7) * mm});
            skArc(sketch, "E116", {"start": v(80, -59.7) * mm, "mid": v(78, -61.7) * mm, "end": v(76, -59.7) * mm});
            skArc(sketch, "E117", {"start": v(120, -59.7) * mm, "mid": v(122, -61.7) * mm, "end": v(124, -59.7) * mm});
            skLineSegment(sketch, "E118.MirrorCS", {"start": v(235.85, -59.7) * mm, "end": v(179.93, -59.7) * mm});
            skLineSegment(sketch, "E119.MirrorCS", {"start": v(239.85, -59.7) * mm, "end": v(239.85, -47.7) * mm});
            skLineSegment(sketch, "E120.MirrorCS", {"start": v(279.85, -47.7) * mm, "end": v(239.85, -47.7) * mm});
            skLineSegment(sketch, "E121.MirrorCS", {"start": v(279.85, -59.7) * mm, "end": v(279.85, -47.7) * mm});
            skLineSegment(sketch, "E122.MirrorCS", {"start": v(359.85, -59.7) * mm, "end": v(283.85, -59.7) * mm});
            skLineSegment(sketch, "E123.MirrorCS", {"start": v(359.85, -273.7) * mm, "end": v(359.85, -59.7) * mm});
            skArc(sketch, "E124.MirrorCS", {"start": v(239.85, -59.7) * mm, "mid": v(237.85, -61.7) * mm, "end": v(235.85, -59.7) * mm});
            skArc(sketch, "E125.MirrorCS", {"start": v(279.85, -59.7) * mm, "mid": v(281.85, -61.7) * mm, "end": v(283.85, -59.7) * mm});
            skLineSegment(sketch, "E126.MirrorCS", {"start": v(0, -273.7) * mm, "end": v(0, -487.7) * mm});
            skLineSegment(sketch, "E127.MirrorCS", {"start": v(0, -487.7) * mm, "end": v(76, -487.7) * mm});
            skArc(sketch, "E128.MirrorCS", {"start": v(80, -487.7) * mm, "mid": v(78, -485.7) * mm, "end": v(76, -487.7) * mm});
            skLineSegment(sketch, "E129.MirrorCS", {"start": v(80, -487.7) * mm, "end": v(80, -499.7) * mm});
            skLineSegment(sketch, "E130.MirrorCS", {"start": v(80, -499.7) * mm, "end": v(120, -499.7) * mm});
            skLineSegment(sketch, "E131.MirrorCS", {"start": v(120, -487.7) * mm, "end": v(120, -499.7) * mm});
            skArc(sketch, "E132.MirrorCS", {"start": v(120, -487.7) * mm, "mid": v(122, -485.7) * mm, "end": v(124, -487.7) * mm});
            skLineSegment(sketch, "E133.MirrorCS", {"start": v(124, -487.7) * mm, "end": v(179.93, -487.7) * mm});
            skLineSegment(sketch, "E134.MirrorCS", {"start": v(235.85, -487.7) * mm, "end": v(179.93, -487.7) * mm});
            skArc(sketch, "E135.MirrorCS", {"start": v(239.85, -487.7) * mm, "mid": v(237.85, -485.7) * mm, "end": v(235.85, -487.7) * mm});
            skLineSegment(sketch, "E136.MirrorCS", {"start": v(239.85, -487.7) * mm, "end": v(239.85, -499.7) * mm});
            skLineSegment(sketch, "E137.MirrorCS", {"start": v(279.85, -499.7) * mm, "end": v(239.85, -499.7) * mm});
            skLineSegment(sketch, "E138.MirrorCS", {"start": v(279.85, -487.7) * mm, "end": v(279.85, -499.7) * mm});
            skArc(sketch, "E139.MirrorCS", {"start": v(279.85, -487.7) * mm, "mid": v(281.85, -485.7) * mm, "end": v(283.85, -487.7) * mm});
            skLineSegment(sketch, "E140.MirrorCS", {"start": v(359.85, -487.7) * mm, "end": v(283.85, -487.7) * mm});
            skLineSegment(sketch, "E141.MirrorCS", {"start": v(359.85, -273.7) * mm, "end": v(359.85, -487.7) * mm});
            skLineSegment(sketch, "E142", {"start": v(80, -53.7) * mm, "end": v(120, -53.7) * mm, "construction": true});
            skCircle(sketch, "E143", {"center": v(100, -53.7) * mm, "radius": 1.75 * mm});
            skCircle(sketch, "E144.MirrorC", {"center": v(259.85, -53.7) * mm, "radius": 1.75 * mm});
            skCircle(sketch, "E145.MirrorC", {"center": v(100, -493.7) * mm, "radius": 1.75 * mm});
            skCircle(sketch, "E146.MirrorC", {"center": v(259.85, -493.7) * mm, "radius": 1.75 * mm});
            skSolve(sketch);
        }
        {
            var Q0;
            Q0=makeQuery(id+"F2.imprint","IMPRINT",FACE,{"disambiguationData":[TD([[makeQuery(id+"F2.imprint","IMPRINT",EDGE,{"derivedFrom":sQuery(id+"F2.wireOp",EDGE,"E110")}),-1.0]])]});
            extrude(context, id + "F3", {"entities" : qUnion([Q0]), "depth" : 12 * mm, "offsetDistance" : 25 * mm});
        }
    });
